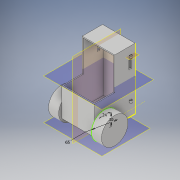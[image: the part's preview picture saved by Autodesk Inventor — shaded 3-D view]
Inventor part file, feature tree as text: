
AUTODESK INVENTOR PART (.ipt)
format: ipt  version: 2018 (Build 220112000, 112)  size: 220,672 bytes
history: native  units: mm
features: extrude x9, sketch x4, plane x4, mirror x3, other x1
ambient origin geometry x8: Origin, YZ Plane, XZ Plane, XY Plane, X Axis, Y Axis, Z Axis, Center Point
bodies: Body1 (feature_tree)
feature tree (21):
  other  "Sólido1"
  extrude  "Extrusión1"  Depth=150.0mm
  extrude  "Extrusión2"  Depth=50.0mm TaperAngle=0.0deg
  sketch  "Boceto2"  dims[d0=80.0mm d1=150.0mm]
  extrude  "Extrusión3"  Depth=65.0mm
  extrude  "Extrusión4"  Depth=30.0mm
  mirror  "Simetría1"
  sketch  "Boceto3"  dims[d2=2.5mm d3=50.0mm d4=0.0mm]
  extrude  "Extrusión5"  Depth=10.0mm TaperAngle=0.0deg
  extrude  "Extrusión6"  Depth=25.0mm TaperAngle=0.0deg
  extrude  "Extrusión7"  Depth=50.0mm
  plane  "Plano de trabajo1"
  sketch  "Boceto4"  dims[d5=0.5mm d6=0.0mm d9=65.0mm]
  plane  "Plano de trabajo2"
  extrude  "Extrusión8"  Depth=80.0mm
  plane  "Plano de trabajo3"
  mirror  "Simetría2"
  extrude  "Extrusión9"  Depth=47.5mm
  plane  "Plano de trabajo4"
  mirror  "Simetría3"
  sketch  "Boceto5"  dims[d15=24.0mm d16=30.0mm d18=10.0mm d19=0.0mm d20=25.0mm d21=0.0mm d24=50.0mm d25=80.0mm d26=47.5mm d27=75.0mm d28=70.0mm d29=0.0mm d30=0.5mm d31=0.0mm d32=0.5mm d35=80.0mm d36=0.0mm d39=100.0mm d40=2.0mm d41=6.0mm d42=5.0mm d43=0.0mm d44=90.0deg d45=24.0mm d46=10.0mm d47=8.0mm d49=20.0mm d50=5.0mm d51=0.0mm d53=6.0mm]
